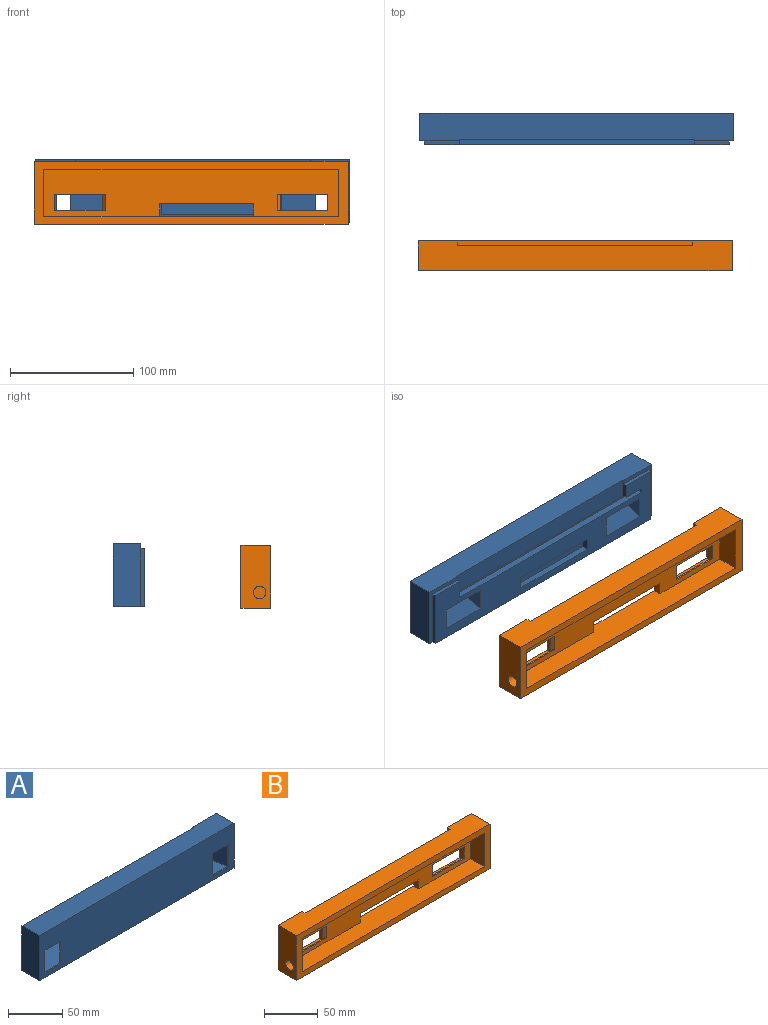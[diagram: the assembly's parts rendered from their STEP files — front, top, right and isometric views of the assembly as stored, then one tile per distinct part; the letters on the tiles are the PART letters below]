
ASSEMBLY  parts=2 mates=1
PART A: 44 faces, bbox 254x25.4x50.8 mm
  f0: plane 254x25.4mm, normal (0,0,-1), area 6429.9mm2, adj f2,f4,f6,f28,f39,f40,f41,f43
  f1: plane 19.05x5.59mm, normal (-1,0,0), area 67.4mm2, adj f2,f3,f5,f8,f9,f10,f42,f43
  f2: plane 246.89x47.24mm, normal (0,1,0), area 6458.3mm2, adj f0,f1,f7,f8,f11,f12,f13,f14
  f3: plane 190.5x15.88mm, normal (0,1,0), area 3024.2mm2, adj f1,f5,f7,f9,f35
  f4: plane 50.8x22.35mm, normal (1,0,0), area 1135.5mm2, adj f0,f5,f28,f43
  f5: plane 254x22.35mm, normal (0,0,1), area 5532.2mm2, adj f1,f3,f4,f6,f7,f28,f40,f43
  f6: plane 50.8x22.35mm, normal (-1,0,0), area 1135.5mm2, adj f0,f5,f28,f40
  f7: plane 15.24x3.81mm, normal (1,0,0), area 47.2mm2, adj f2,f3,f5,f36,f38,f40
  f8: plane 208.28x5.59mm, normal (0,0,1), area 1163.9mm2, adj f1,f2,f10,f37
  f9: plane 190.5x1.78mm, normal (0,0,-1), area 338.7mm2, adj f1,f3,f10,f35
  f10: plane 208.28x3.81mm, normal (0,1,0), area 672.6mm2, adj f1,f8,f9,f35,f36,f37
  f11: plane 55.88x24.13mm, normal (0,-0.15,-0.99), area 1152.3mm2, adj f2,f12,f14,f23,f29
  f12: plane 25.4x24.13mm, normal (0.94,-0.34,0), area 559.8mm2, adj f2,f11,f13,f27
  f13: plane 55.88x24.13mm, normal (0,-0.15,0.99), area 1152.3mm2, adj f2,f12,f14,f25,f29
  f14: plane 25.4x24.13mm, normal (-0.94,-0.34,0), area 559.8mm2, adj f2,f11,f13,f29
  f15: plane 25.4x24.13mm, normal (-0.94,-0.34,0), area 559.8mm2, adj f2,f16,f18,f22
  f16: plane 55.88x24.13mm, normal (0,-0.15,0.99), area 1152.3mm2, adj f2,f15,f17,f19,f26
  f17: plane 25.4x24.13mm, normal (0.94,-0.34,0), area 559.8mm2, adj f2,f16,f18,f19
  f18: plane 55.88x24.13mm, normal (0,-0.15,-0.99), area 1152.3mm2, adj f2,f15,f17,f19,f21
  f19: plane 35.56x25.4mm, normal (0,1,0), area 903.2mm2, adj f16,f17,f18,f20
  f20: plane 25.4x1.27mm, normal (1,0,0), area 32.3mm2, adj f19,f21,f26,f28
  f21: plane 20.32x1.27mm, normal (0,0,-1), area 25.8mm2, adj f18,f20,f22,f28
  f22: plane 25.4x1.27mm, normal (-1,0,0), area 32.3mm2, adj f15,f21,f26,f28
  f23: plane 20.32x1.27mm, normal (0,0,-1), area 25.8mm2, adj f11,f24,f27,f28
  f24: plane 25.4x1.27mm, normal (-1,0,0), area 32.3mm2, adj f23,f25,f28,f29
  f25: plane 20.32x1.27mm, normal (0,0,1), area 25.8mm2, adj f13,f24,f27,f28
  f26: plane 20.32x1.27mm, normal (0,0,1), area 25.8mm2, adj f16,f20,f22,f28
  f27: plane 25.4x1.27mm, normal (1,0,0), area 32.3mm2, adj f12,f23,f25,f28
  f28: plane 254x50.8mm, normal (0,-1,0), area 11870.9mm2, adj f0,f4,f5,f6,f20,f21,f22,f23
  f29: plane 35.56x25.4mm, normal (0,1,0), area 903.2mm2, adj f11,f13,f14,f24
  f30: plane 76.2x5.08mm, normal (0,0,-1), area 387.1mm2, adj f2,f31,f33,f34
  f31: plane 10.16x5.08mm, normal (-1,0,0), area 51.6mm2, adj f2,f30,f32,f34
  f32: plane 76.2x5.08mm, normal (0,0,1), area 387.1mm2, adj f2,f31,f33,f34
  f33: plane 10.16x5.08mm, normal (1,0,0), area 51.6mm2, adj f2,f30,f32,f34
  f34: plane 76.2x10.16mm, normal (0,1,0), area 774.2mm2, adj f30,f31,f32,f33
  f35: plane 1.78x0.64mm, normal (-1,0,0), area 1.1mm2, adj f3,f9,f10,f36
  f36: plane 17.78x5.59mm, normal (0,0,-1), area 99.4mm2, adj f2,f7,f10,f35,f37
  f37: plane 5.59x3.81mm, normal (1,0,0), area 21.3mm2, adj f2,f8,f10,f36
  f38: plane 28.19x3.05mm, normal (0,0,1), area 85.9mm2, adj f2,f7,f39,f40
  f39: plane 47.24x3.05mm, normal (-1,0,0), area 144mm2, adj f0,f2,f38,f40
  f40: plane 50.8x31.75mm, normal (0,1,0), area 280.9mm2, adj f0,f5,f6,f7,f38,f39
  f41: plane 47.24x3.05mm, normal (1,0,0), area 144mm2, adj f0,f2,f42,f43
  f42: plane 28.19x3.05mm, normal (0,0,1), area 85.9mm2, adj f1,f2,f41,f43
  f43: plane 50.8x31.75mm, normal (0,1,0), area 280.9mm2, adj f0,f1,f4,f5,f41,f42
PART B: 39 faces, bbox 254x24.1x50.8 mm
  f0: plane 18.29x3.81mm, normal (1,0,0), area 69.7mm2, adj f2,f7,f8,f37
  f1: plane 18.29x6.35mm, normal (1,0,0), area 109.7mm2, adj f2,f4,f6,f24,f28,f29,f30,f31
  f2: plane 254x50.8mm, normal (0,1,0), area 7087.9mm2, adj f0,f1,f4,f5,f6,f7,f8,f9
  f3: plane 254x50.8mm, normal (0,-1,0), area 3806.4mm2, adj f11,f12,f13,f14,f20,f21,f22,f23
  f4: plane 39.88x5.08mm, normal (0,0,-1), area 196.9mm2, adj f1,f2,f5,f29,f36
  f5: plane 18.29x3.81mm, normal (-1,0,0), area 69.7mm2, adj f2,f4,f6,f36
  f6: plane 39.88x5.08mm, normal (0,0,1), area 196.9mm2, adj f1,f2,f5,f31,f36
  f7: plane 39.88x5.08mm, normal (0,0,1), area 196.9mm2, adj f0,f2,f9,f35,f37
  f8: plane 39.88x5.08mm, normal (0,0,-1), area 196.9mm2, adj f0,f2,f9,f33,f37
  f9: plane 18.29x6.35mm, normal (-1,0,0), area 109.7mm2, adj f2,f7,f8,f24,f32,f33,f34,f35
  f10: plane 190.5x15.88mm, normal (0,1,0), area 3024.2mm2, adj f13,f15,f16,f18
  f11: plane 254x24.13mm, normal (0,0,-1), area 6129mm2, adj f2,f3,f12,f14
  f12: plane 50.8x24.13mm, normal (1,0,0), area 1225.8mm2, adj f2,f3,f11,f13
  f13: plane 254x24.13mm, normal (0,0,1), area 5403.2mm2, adj f2,f3,f10,f12,f14,f15,f16
  f14: plane 50.8x24.13mm, normal (-1,0,0), area 1144.7mm2, adj f2,f3,f11,f13,f38
  f15: plane 19.05x5.59mm, normal (-1,0,0), area 78.2mm2, adj f2,f10,f13,f17,f18,f19
  f16: plane 19.05x5.59mm, normal (1,0,0), area 78.2mm2, adj f2,f10,f13,f17,f18,f19
  f17: plane 190.5x5.59mm, normal (0,0,1), area 1064.5mm2, adj f2,f15,f16,f19
  f18: plane 190.5x1.78mm, normal (0,0,-1), area 338.7mm2, adj f10,f15,f16,f19
  f19: plane 190.5x3.18mm, normal (0,1,0), area 604.8mm2, adj f15,f16,f17,f18
  f20: plane 38.1x17.78mm, normal (1,0,0), area 596.3mm2, adj f3,f21,f23,f24,f38
  f21: plane 238.76x24.13mm, normal (0,0,1), area 4729mm2, adj f2,f3,f20,f22,f24,f25,f26
  f22: plane 38.1x17.78mm, normal (-1,0,0), area 677.4mm2, adj f3,f21,f23,f24
  f23: plane 238.76x17.78mm, normal (0,0,-1), area 4245.2mm2, adj f3,f20,f22,f24
  f24: plane 238.76x38.1mm, normal (0,-1,0), area 7235.6mm2, adj f1,f9,f20,f21,f22,f23,f25,f26
  f25: plane 10.16x6.35mm, normal (1,0,0), area 64.5mm2, adj f2,f21,f24,f27
  f26: plane 10.16x6.35mm, normal (-1,0,0), area 64.5mm2, adj f2,f21,f24,f27
  f27: plane 76.2x6.35mm, normal (0,0,-1), area 483.9mm2, adj f2,f24,f25,f26
  f28: plane 41.15x1.27mm, normal (0,0,-1), area 51.5mm2, adj f1,f24,f29,f36
  f29: plane 39.88x2.54mm, normal (0,1,0), area 101.3mm2, adj f1,f4,f28,f36
  f30: plane 41.15x1.27mm, normal (0,0,1), area 51.5mm2, adj f1,f24,f31,f36
  f31: plane 39.88x2.54mm, normal (0,1,0), area 101.3mm2, adj f1,f6,f30,f36
  f32: plane 41.15x1.27mm, normal (0,0,-1), area 51.5mm2, adj f9,f24,f33,f37
  f33: plane 39.88x2.54mm, normal (0,1,0), area 101.3mm2, adj f8,f9,f32,f37
  f34: plane 41.15x1.27mm, normal (0,0,1), area 51.5mm2, adj f9,f24,f35,f37
  f35: plane 39.88x2.54mm, normal (0,1,0), area 101.3mm2, adj f7,f9,f34,f37
  f36: plane 18.29x2.54mm, normal (-0.71,-0.71,0), area 56.6mm2, adj f4,f5,f6,f24,f28,f29,f30,f31
  f37: plane 18.29x2.54mm, normal (0.71,-0.71,0), area 56.6mm2, adj f0,f7,f8,f24,f32,f33,f34,f35
  f38: cylinder r=5.08mm len=10.16mm, axis (1,0,0), area 243.2mm2, adj f14,f20
PLACE A rot(axis=(0,0,1),180deg) t=(-10.1,61.67,-57.92)mm
PLACE B t=(-11.32,-16.3,-59.24)mm
MATE slider A.f2 <-> B.f2  axis (0,-1,0) through (-12.71,61.67,-64.32)mm
